FCSTD DOCUMENT  (FreeCAD 1.0R39285 (Git))
Label: WinkelTestZeichnung
License: All rights reserved
objects: Part::Part2DObjectPython×7, TechDraw::DrawRichAnno×3, TechDraw::DrawSVGTemplate×1, Part::Mirroring×1, App::DocumentObjectGroup×1, TechDraw::DrawViewDraft×1, TechDraw::DrawPage×1
note: 8 computed .brp shape members not serialized (recipe doc carries the construction recipe); baked Part::Feature solids carry a one-line shape summary decoded from their .brp

FEATURE [Part::Part2DObjectPython] Circle  # Draft 2D object (typed FeaturePython)
  Area = 0
  FirstAngle = 0
  LastAngle = 0
  MakeFace = false
  Radius = 8
FEATURE [Part::Part2DObjectPython] Line  # Draft 2D object (typed FeaturePython)
  Area = 0
  ChamferSize = 0
  Closed = false
  End = (-100,-8.8e-15,0)
  FilletRadius = 0
  Length = 200
  MakeFace = false
  Placement = pos=(-160,-1.47e-14,0) rot=(0,0,1;0rad)
  Points = (2) [(260,2.05333e-14,0),(60,5.86667e-15,0)]
  Start = (100,5.8e-15,0)
  Subdivisions = 0
FEATURE [Part::Part2DObjectPython] Circle001  # Draft 2D object (typed FeaturePython)
  Area = 0
  FirstAngle = 0
  LastAngle = 0
  MakeFace = false
  Radius = 51
FEATURE [Part::Part2DObjectPython] Line008  # Draft 2D object (typed FeaturePython)
  Area = 0
  ChamferSize = 0
  Closed = false
  End = (0,100,0)
  FilletRadius = 0
  Length = 200
  MakeFace = false
  Placement = pos=(0,-1.3e-15,0) rot=(0,0,1;0rad)
  Points = (2) [(0,-100,0),(0,100,0)]
  Start = (0,-100,0)
  Subdivisions = 0
FEATURE [TechDraw::DrawSVGTemplate] Template
  Height = 210
  Orientation = 1
  Template = C:/Program Files/FreeCAD/data/Mod/TechDraw/Templates/Default_Template_A4_Landscape.svg
  Width = 297
FEATURE [Part::Mirroring] Mirror  label="Line007 (mirrored)"
  Base = (0,75,0)
  Normal = (-1,0,0)
FEATURE [Part::Part2DObjectPython] Circle003  # Draft 2D object (typed FeaturePython)
  Area = 0
  FirstAngle = 0
  LastAngle = 0
  MakeFace = false
  Placement = pos=(0,-1.7e-15,0) rot=(0,0,1;0rad)
  Radius = 100
FEATURE [TechDraw::DrawRichAnno] RichTextAnnotation
  AnnoText = <!DOCTYPE HTML PUBLIC "-//W3C//DTD HTML 4.0//EN" "http://www.w3.org/TR/REC-html40/strict.dtd">\n<html><head><meta name="qrichtext" content="1" /><style type="text/css">\np, li { white-space: pre-wrap; }\n</style></head><body style=" font-family:'osifont'; font-size:7.8pt; font-weight:400; font-style:normal;">\n<p style=" margin-top:0px; margin-bottom:0px; margin-left:0px; margin-right:0px; -qt-block-indent:0; text-indent:0px;"><span style=" font-family:'MS Shell Dlg 2'; font-size:18pt;">40°</span></p></body></html>
  LockPosition = false
  MaxWidth = -1
  Rotation = 0
  ScaleType = 2
  ShowFrame = false
  X = 82.2208
  Y = 160.617
FEATURE [TechDraw::DrawRichAnno] RichTextAnnotation001
  AnnoText = <!DOCTYPE HTML PUBLIC "-//W3C//DTD HTML 4.0//EN" "http://www.w3.org/TR/REC-html40/strict.dtd">\n<html><head><meta name="qrichtext" content="1" /><style type="text/css">\np, li { white-space: pre-wrap; }\n</style></head><body style=" font-family:'osifont'; font-size:7.8pt; font-weight:400; font-style:normal;">\n<p style=" margin-top:0px; margin-bottom:0px; margin-left:0px; margin-right:0px; -qt-block-indent:0; text-indent:0px;"><span style=" font-family:'MS Shell Dlg 2'; font-size:18pt;">40°</span></p></body></html>
  LockPosition = false
  MaxWidth = -1
  Rotation = 0
  ScaleType = 2
  ShowFrame = false
  X = 219.855
  Y = 161.326
FEATURE [TechDraw::DrawRichAnno] RichTextAnnotation002
  AnnoText = <!DOCTYPE HTML PUBLIC "-//W3C//DTD HTML 4.0//EN" "http://www.w3.org/TR/REC-html40/strict.dtd">\n<html><head><meta name="qrichtext" content="1" /><style type="text/css">\np, li { white-space: pre-wrap; }\n</style></head><body style=" font-family:'osifont'; font-size:7.8pt; font-weight:400; font-style:normal;">\n<p style=" margin-top:0px; margin-bottom:0px; margin-left:0px; margin-right:0px; -qt-block-indent:0; text-indent:0px;"><span style=" font-family:'MS Shell Dlg 2'; font-size:18pt;">0°</span></p></body></html>
  LockPosition = false
  MaxWidth = -1
  Rotation = 0
  ScaleType = 2
  ShowFrame = false
  X = 148.969
  Y = 190.787
FEATURE [Part::Part2DObjectPython] Line009  # Draft 2D object (typed FeaturePython)
  Area = 0
  ChamferSize = 0
  Closed = true
  End = (-64.2788,76.6044,0)
  FilletRadius = 0
  Length = 200
  MakeFace = false
  Placement = pos=(0,0,0) rot=(0,0,1;0.698132rad)
  Points = (2) [(-3.90799e-13,-100,0),(1.49214e-13,100,0)]
  Start = (64.2788,-76.6044,0)
  Subdivisions = 0
FEATURE [Part::Part2DObjectPython] Line010  # Draft 2D object (typed FeaturePython)
  Area = 0
  ChamferSize = 0
  Closed = true
  End = (-98.4808,17.3648,0)
  FilletRadius = 0
  Length = 200
  MakeFace = false
  Placement = pos=(1.99e-13,1.137e-13,0) rot=(0,0,1;1.39626rad)
  Points = (2) [(-3.90799e-13,-100,0),(1.49214e-13,100,0)]
  Start = (98.4808,-17.3648,0)
  Subdivisions = 0
FEATURE [App::DocumentObjectGroup] Group
  Group = -> [Circle,Circle001,Circle003,Line008,Line009,Line,Line010,Mirror]
FEATURE [TechDraw::DrawViewDraft] DraftView
  Direction = (0,0,1)
  FontSize = 80
  LineSpacing = 1
  LineStyle = Solid
  LineWidth = 0.2
  LockPosition = true
  OverrideStyle = false
  Rotation = 0
  ScaleType = 2
  Source = -> Group
  Symbol = <blob: 2329 chars omitted>
  X = 150.195
  Y = 80.0262
FEATURE [TechDraw::DrawPage] Page
  KeepUpdated = true
  NextBalloonIndex = 1
  ProjectionType = 0
  Template = -> Template
  Views = -> [DraftView,RichTextAnnotation,RichTextAnnotation001,RichTextAnnotation002]
